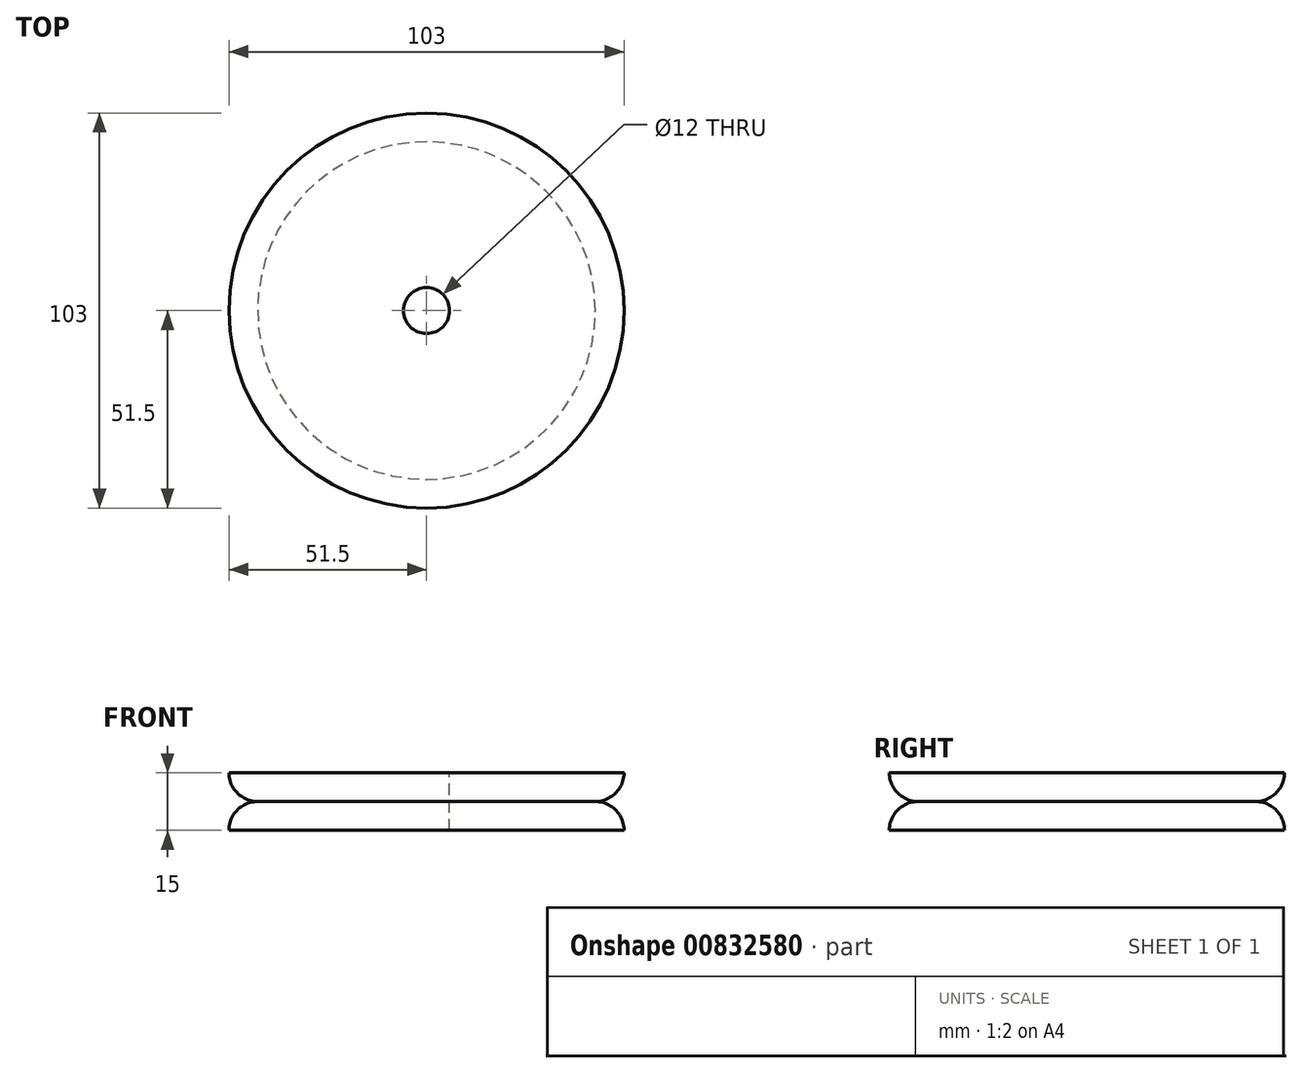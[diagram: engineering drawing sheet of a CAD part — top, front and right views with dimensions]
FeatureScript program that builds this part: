
annotation { "Feature Type Name" : "Feature", "Feature Type Description" : "" }
export const myFeature = defineFeature(function(context is Context, id is Id, definition is map)
    precondition{}
    {
        {
            var Q0;
            Q0=qCreatedBy(makeId("Top.planeOp"),FACE);
            var sketch = newSketch(context, id + "F0", { "sketchPlane" : qUnion([Q0])});
            skCircle(sketch, "E0", {"center": v(0, 0) * mm, "radius": 51.5 * mm});
            skSolve(sketch);
        }
        {
            var Q0;
            Q0=makeQuery(id+"F0.imprint","IMPRINT",FACE,{"disambiguationData":[TD([[makeQuery(id+"F0.imprint","IMPRINT",EDGE,{"derivedFrom":sQuery(id+"F0.wireOp",EDGE,"E0")}),1.0]])]});
            extrude(context, id + "F1", {"entities" : qUnion([Q0]), "depth" : 7.5 * mm, "offsetDistance" : 25 * mm});
        }
        {
            var Q0;
            Q0=makeQuery(id+"F1.opExtrude","CAP_EDGE",EDGE,{"disambiguationData":[OSD([sQuery(id+"F0.wireOp",EDGE,"E0")])],"isStart":false});
            fillet(context, id + "F2", {"entities" : qUnion([Q0]), "radius" : 7.5 * mm, "tangentPropagation" : true, "allowEdgeOverflow" : false});
        }
        {
            var Q0;
            Q0=makeQuery(id+"F1.opExtrude","CAP_FACE",FACE,{"disambiguationData":[OSD([sQuery(id+"F0.wireOp",EDGE,"E0")])],"isStart":false});
            var sketch = newSketch(context, id + "F3", { "sketchPlane" : qUnion([Q0])});
            skCircle(sketch, "E1", {"center": v(0, 0) * mm, "radius": 51.5 * mm});
            skSolve(sketch);
        }
        {
            var Q0;
            Q0=makeQuery(id+"F3.imprint","IMPRINT",FACE,{"disambiguationData":[TD([[makeQuery(id+"F3.imprint","IMPRINT",EDGE,{"derivedFrom":sQuery(id+"F3.wireOp",EDGE,"E1")}),1.0]])]});
            var Q1;
            {var subQ0=sQuery(id+"F0.wireOp",EDGE,"E0");Q1=makeQuery(id+"F3.imprint","IMPRINT",FACE,{"disambiguationData":[TD([[makeQuery(id+"F3.imprint","IMPRINT",EDGE,{"derivedFrom":makeQuery(id+"F2.opFillet","BLEND_EDGE",EDGE,{"blendedFrom":[makeQuery(id+"F1.opExtrude","CAP_EDGE",EDGE,{"disambiguationData":[OSD([subQ0])],"isStart":false}),makeQuery(id+"F1.opExtrude","CAP_FACE",FACE,{"disambiguationData":[OSD([subQ0])],"isStart":false})],"blendedInto":[makeQuery(id+"F1.opExtrude","CAP_FACE",FACE,{"disambiguationData":[OSD([subQ0])],"isStart":false})]})}),1.0]])]});}
            extrude(context, id + "F4", {"entities" : qUnion([Q0, Q1]), "operationType" : NewBodyOperationType.ADD, "depth" : 7.5 * mm, "offsetDistance" : 25 * mm});
        }
        {
            var Q0;
            Q0=makeQuery(id+"F4.opExtrude","CAP_EDGE",EDGE,{"disambiguationData":[OSD([sQuery(id+"F3.wireOp",EDGE,"E1")])],"isStart":true});
            fillet(context, id + "F5", {"entities" : qUnion([Q0]), "radius" : 7.5 * mm, "tangentPropagation" : true, "allowEdgeOverflow" : false});
        }
        {
            var Q0;
            Q0=makeQuery(id+"F4.opExtrude","CAP_FACE",FACE,{"disambiguationData":[OSD([sQuery(id+"F3.wireOp",EDGE,"E1")])],"isStart":false});
            var sketch = newSketch(context, id + "F6", { "sketchPlane" : qUnion([Q0])});
            skCircle(sketch, "E2", {"center": v(0, 0) * mm, "radius": 6 * mm});
            skSolve(sketch);
        }
        {
            var Q0;
            Q0=makeQuery(id+"F6.imprint","IMPRINT",FACE,{"disambiguationData":[TD([[makeQuery(id+"F6.imprint","IMPRINT",EDGE,{"derivedFrom":sQuery(id+"F6.wireOp",EDGE,"E2")}),1.0]])]});
            extrude(context, id + "F7", {"entities" : qUnion([Q0]), "operationType" : NewBodyOperationType.REMOVE, "oppositeDirection" : true, "depth" : 25 * mm, "offsetDistance" : 25 * mm});
        }
    });
